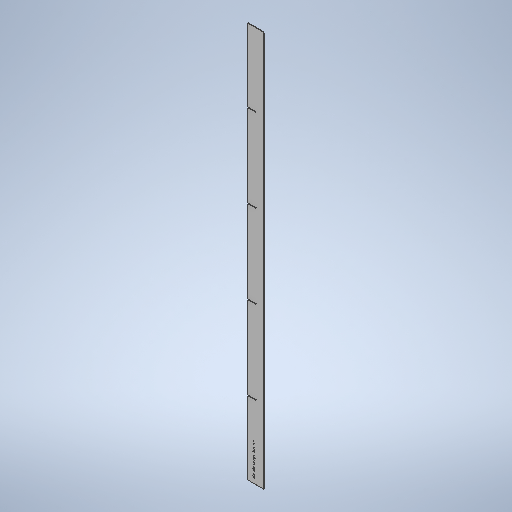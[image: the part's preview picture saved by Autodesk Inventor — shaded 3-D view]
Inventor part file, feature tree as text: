
AUTODESK INVENTOR PART (.ipt)
format: ipt  version: 2025 (Build 290162010, 162A)  size: 452,608 bytes
history: native  units: mm
features: other x4, sketch x3, sheet_metal_op x1, extrude x1, pattern_linear x1, projected_geometry x1
ambient origin geometry x8: Origin, YZ Plane, XZ Plane, XY Plane, X Axis, Y Axis, Z Axis, Center Point
bodies: Body1 (feature_tree)
feature tree (11):
  sheet_metal_op  "Face2"
  extrude  "Extrusion2"  Depth=2380.0mm
  pattern_linear  "Rectangular Pattern1"  Spacing1=3.2mm  [1 undecoded]
  other  "Corner Chamfer1"
  other  "Mark1"
  sketch  "Sketch6"  dims[d26=95.0mm d27=2380.0mm]
  other  "Plate4"
  sketch  "Sketch7"  dims[d28=3.0mm]
  projected_geometry  "Projected Loop1"
  sketch  "Sketch8"  dims[d29=48.5mm d30=3.2mm d31=439.437mm d32=0.0mm d33=0.0mm d34=50.0mm d36=500.0mm d37=6.0mm d38=6.0mm d39=45.0deg]
  other  "Definition1"
note: 1 required parameter value undecoded (feature->parameter linkage not recoverable at this tier; creation-order binding heuristic only, values carry confidence <= 0.55)
